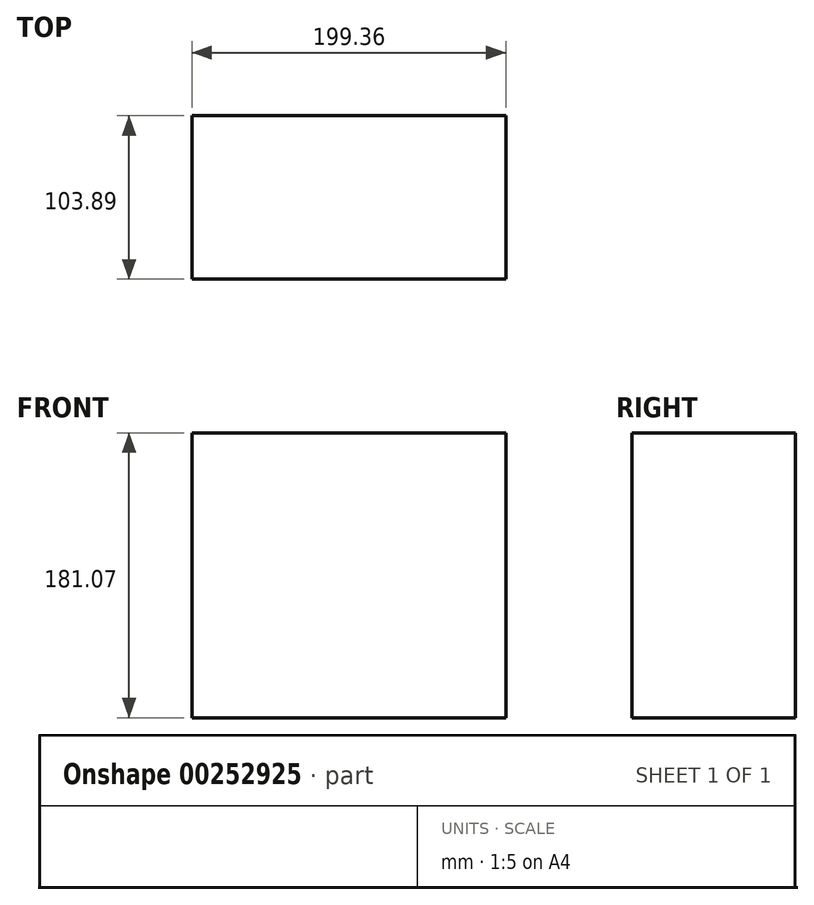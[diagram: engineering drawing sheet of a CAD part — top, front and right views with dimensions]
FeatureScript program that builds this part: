
annotation { "Feature Type Name" : "Feature", "Feature Type Description" : "" }
export const myFeature = defineFeature(function(context is Context, id is Id, definition is map)
    precondition{}
    {
        {
            var Q0;
            Q0=qCreatedBy(makeId("Front.planeOp"),FACE);
            var sketch = newSketch(context, id + "F0", { "sketchPlane" : qUnion([Q0])});
            skLineSegment(sketch, "E0.bottom", {"start": v(-99.68, 4.8) * mm, "end": v(99.68, 4.8) * mm});
            skLineSegment(sketch, "E0.top", {"start": v(-99.68, -75.93) * mm, "end": v(99.68, -75.93) * mm});
            skLineSegment(sketch, "E0.left", {"start": v(-99.68, 4.8) * mm, "end": v(-99.68, -75.93) * mm});
            skLineSegment(sketch, "E0.right", {"start": v(99.68, 4.8) * mm, "end": v(99.68, -75.93) * mm});
            skSolve(sketch);
        }
        {
            var Q0;
            Q0 = qSketchRegion(id + "F0", true);
            extrude(context, id + "F1", {"entities" : qUnion([Q0]), "depth" : 103.89 * mm});
        }
        {
            var Q0;
            Q0=makeQuery(id+"F1.opExtrude","SWEPT_FACE",FACE,{"disambiguationData":[OSD([sQuery(id+"F0.wireOp",EDGE,"E0.top")])]});
            extrude(context, id + "F2", {"entities" : qUnion([Q0]), "operationType" : NewBodyOperationType.ADD, "depth" : 25.4 * mm});
        }
        {
            var Q0;
            Q0=qCreatedBy(makeId("Front.planeOp"),FACE);
            var sketch = newSketch(context, id + "F3", { "sketchPlane" : qUnion([Q0])});
            skSolve(sketch);
        }
        {
            var Q0;
            Q0 = qSketchRegion(id + "F3", true);
            var Q1;
            Q1=makeQuery(id+"F2.opExtrude","CAP_FACE",FACE,{"disambiguationData":[OSD([sQuery(id+"F0.wireOp",EDGE,"E0.top")])],"isStart":false});
            extrude(context, id + "F4", {"entities" : qUnion([Q0, Q1]), "operationType" : NewBodyOperationType.ADD, "depth" : 74.93 * mm});
        }
    });
